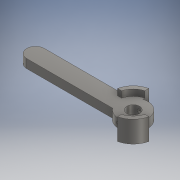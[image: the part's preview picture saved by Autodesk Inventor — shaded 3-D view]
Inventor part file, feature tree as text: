
AUTODESK INVENTOR PART (.ipt)
format: ipt  version: 2018 (Build 220112000, 112)  size: 164,864 bytes
history: native  units: mm
features: extrude x3, sketch x2
ambient origin geometry x8: Origin, YZ Plane, XZ Plane, XY Plane, X Axis, Y Axis, Z Axis, Center Point
bodies: Solid1 (feature_tree)
feature tree (5):
  sketch  "Sketch1"  dims[d0=13.0mm d1=30.0mm]
  extrude  "Extrusion1"  Depth=30.0mm
  extrude  "Extrusion2"  Depth=34.0mm
  extrude  "Extrusion3"  Depth=4.5mm
  sketch  "Sketch2"  dims[d2=42.0mm d3=34.0mm d4=4.5mm d5=4.5mm d6=4.5mm d7=4.5mm d8=100.0mm d9=9.0mm d10=9.0mm d11=0.0mm d12=15.5mm d13=6.5mm d14=0.0mm d15=0.0mm d25=4.5mm d26=4.5mm d27=4.0mm d28=89.0mm d29=0.0mm]
